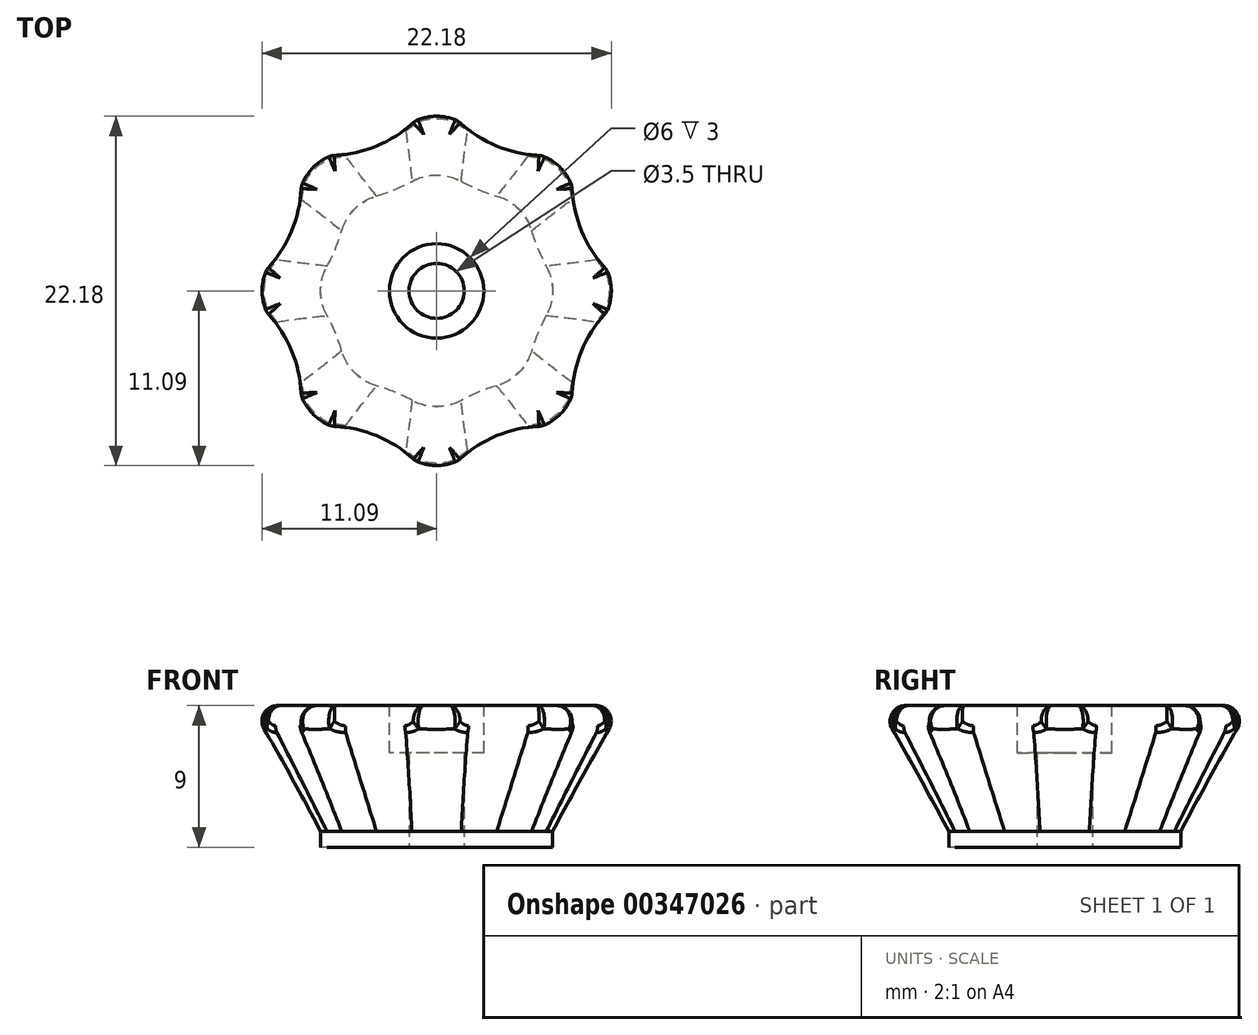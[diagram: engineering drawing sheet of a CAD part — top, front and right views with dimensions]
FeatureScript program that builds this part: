
annotation { "Feature Type Name" : "Feature", "Feature Type Description" : "" }
export const myFeature = defineFeature(function(context is Context, id is Id, definition is map)
    precondition{}
    {
        {
            var Q0;
            Q0=qCreatedBy(makeId("Top.planeOp"),FACE);
            var sketch = newSketch(context, id + "F0", { "sketchPlane" : qUnion([Q0])});
            skArc(sketch, "E0", {"start": v(0, 12.5) * mm, "mid": v(-8.84, 8.84) * mm, "end": v(-12.5, 0) * mm, "construction": true});
            skLineSegment(sketch, "E1", {"start": v(0, 0) * mm, "end": v(0, 89.09) * mm, "construction": true});
            skLineSegment(sketch, "E2", {"start": v(0, 0) * mm, "end": v(-93.87, 0) * mm, "construction": true});
            skArc(sketch, "E3", {"start": v(-8.84, 8.84) * mm, "mid": v(-3.81, 9.2) * mm, "end": v(0, 12.5) * mm});
            skArc(sketch, "E4", {"start": v(-12.5, 0) * mm, "mid": v(-9.2, 3.81) * mm, "end": v(-8.84, 8.84) * mm});
            skArc(sketch, "E5.MirrorCS", {"start": v(12.5, 0) * mm, "mid": v(9.2, 3.81) * mm, "end": v(8.84, 8.84) * mm});
            skArc(sketch, "E6.MirrorCS", {"start": v(8.84, 8.84) * mm, "mid": v(3.81, 9.2) * mm, "end": v(0, 12.5) * mm});
            skArc(sketch, "E7.MirrorCS", {"start": v(-12.5, 0) * mm, "mid": v(-9.2, -3.81) * mm, "end": v(-8.84, -8.84) * mm});
            skArc(sketch, "E8.MirrorCS", {"start": v(-8.84, -8.84) * mm, "mid": v(-3.81, -9.2) * mm, "end": v(0, -12.5) * mm});
            skArc(sketch, "E9.MirrorCS", {"start": v(8.84, -8.84) * mm, "mid": v(3.81, -9.2) * mm, "end": v(0, -12.5) * mm});
            skArc(sketch, "E10.MirrorCS", {"start": v(12.5, 0) * mm, "mid": v(9.2, -3.81) * mm, "end": v(8.84, -8.84) * mm});
            skSolve(sketch);
        }
        {
            var Q0;
            Q0=makeQuery(id+"F0.imprint","IMPRINT",FACE,{"disambiguationData":[TD([[makeQuery(id+"F0.imprint","IMPRINT",EDGE,{"derivedFrom":sQuery(id+"F0.wireOp",EDGE,"E3")}),-1.0]])]});
            extrude(context, id + "F1", {"entities" : qUnion([Q0]), "oppositeDirection" : true, "depth" : 8 * mm});
        }
        {
            var Q0;
            Q0=makeQuery(id+"F1.opExtrude","CAP_FACE",FACE,{"disambiguationData":[OSD([sQuery(id+"F0.wireOp",EDGE,"E3"),sQuery(id+"F0.wireOp",EDGE,"E4"),sQuery(id+"F0.wireOp",EDGE,"E5.MirrorCS"),sQuery(id+"F0.wireOp",EDGE,"E6.MirrorCS"),sQuery(id+"F0.wireOp",EDGE,"E7.MirrorCS"),sQuery(id+"F0.wireOp",EDGE,"E8.MirrorCS"),sQuery(id+"F0.wireOp",EDGE,"E9.MirrorCS"),sQuery(id+"F0.wireOp",EDGE,"E10.MirrorCS")])],"isStart":true});
            var sketch = newSketch(context, id + "F2", { "sketchPlane" : qUnion([Q0])});
            skCircle(sketch, "E11", {"center": v(0, 0) * mm, "radius": 3 * mm});
            skSolve(sketch);
        }
        {
            var Q0;
            Q0=makeQuery(id+"F2.imprint","IMPRINT",FACE,{"disambiguationData":[TD([[makeQuery(id+"F2.imprint","IMPRINT",EDGE,{"derivedFrom":sQuery(id+"F2.wireOp",EDGE,"E11")}),1.0]])]});
            extrude(context, id + "F3", {"entities" : qUnion([Q0]), "operationType" : NewBodyOperationType.REMOVE, "oppositeDirection" : true, "depth" : 3 * mm});
        }
        {
            var Q0;
            Q0=makeQuery(id+"F1.opExtrude","CAP_EDGE",EDGE,{"disambiguationData":[OSD([sQuery(id+"F0.wireOp",EDGE,"E6.MirrorCS")])],"isStart":false});
            var Q1;
            Q1=makeQuery(id+"F1.opExtrude","CAP_EDGE",EDGE,{"disambiguationData":[OSD([sQuery(id+"F0.wireOp",EDGE,"E3")])],"isStart":false});
            var Q2;
            Q2=makeQuery(id+"F1.opExtrude","CAP_EDGE",EDGE,{"disambiguationData":[OSD([sQuery(id+"F0.wireOp",EDGE,"E4")])],"isStart":false});
            var Q3;
            Q3=makeQuery(id+"F1.opExtrude","CAP_EDGE",EDGE,{"disambiguationData":[OSD([sQuery(id+"F0.wireOp",EDGE,"E7.MirrorCS")])],"isStart":false});
            var Q4;
            Q4=makeQuery(id+"F1.opExtrude","CAP_EDGE",EDGE,{"disambiguationData":[OSD([sQuery(id+"F0.wireOp",EDGE,"E8.MirrorCS")])],"isStart":false});
            var Q5;
            Q5=makeQuery(id+"F1.opExtrude","CAP_EDGE",EDGE,{"disambiguationData":[OSD([sQuery(id+"F0.wireOp",EDGE,"E10.MirrorCS")])],"isStart":false});
            var Q6;
            Q6=makeQuery(id+"F1.opExtrude","CAP_EDGE",EDGE,{"disambiguationData":[OSD([sQuery(id+"F0.wireOp",EDGE,"E9.MirrorCS")])],"isStart":false});
            var Q7;
            Q7=makeQuery(id+"F1.opExtrude","CAP_EDGE",EDGE,{"disambiguationData":[OSD([sQuery(id+"F0.wireOp",EDGE,"E5.MirrorCS")])],"isStart":false});
            chamfer(context, id + "F4", {"entities" : qUnion([Q0, Q1, Q2, Q3, Q4, Q5, Q6, Q7]), "chamferType" : ChamferType.TWO_OFFSETS, "width1" : 3 * mm, "oppositeDirection" : false, "width2" : 6.5 * mm, "tangentPropagation" : true});
        }
        {
            var Q0;
            Q0=makeQuery(id+"F1.opExtrude","SWEPT_EDGE",EDGE,{"disambiguationData":[OSD([sQuery(id+"F0.wireOp",EDGE,"E4"),sQuery(id+"F0.wireOp",EDGE,"E7.MirrorCS")])]});
            var Q1;
            Q1=makeQuery(id+"F1.opExtrude","SWEPT_EDGE",EDGE,{"disambiguationData":[OSD([sQuery(id+"F0.wireOp",EDGE,"E7.MirrorCS"),sQuery(id+"F0.wireOp",EDGE,"E8.MirrorCS")])]});
            var Q2;
            Q2=makeQuery(id+"F1.opExtrude","SWEPT_EDGE",EDGE,{"disambiguationData":[OSD([sQuery(id+"F0.wireOp",EDGE,"E8.MirrorCS"),sQuery(id+"F0.wireOp",EDGE,"E9.MirrorCS")])]});
            var Q3;
            Q3=makeQuery(id+"F1.opExtrude","SWEPT_EDGE",EDGE,{"disambiguationData":[OSD([sQuery(id+"F0.wireOp",EDGE,"E9.MirrorCS"),sQuery(id+"F0.wireOp",EDGE,"E10.MirrorCS")])]});
            var Q4;
            Q4=makeQuery(id+"F1.opExtrude","SWEPT_EDGE",EDGE,{"disambiguationData":[OSD([sQuery(id+"F0.wireOp",EDGE,"E5.MirrorCS"),sQuery(id+"F0.wireOp",EDGE,"E10.MirrorCS")])]});
            var Q5;
            Q5=makeQuery(id+"F1.opExtrude","SWEPT_EDGE",EDGE,{"disambiguationData":[OSD([sQuery(id+"F0.wireOp",EDGE,"E5.MirrorCS"),sQuery(id+"F0.wireOp",EDGE,"E6.MirrorCS")])]});
            var Q6;
            Q6=makeQuery(id+"F1.opExtrude","SWEPT_EDGE",EDGE,{"disambiguationData":[OSD([sQuery(id+"F0.wireOp",EDGE,"E3"),sQuery(id+"F0.wireOp",EDGE,"E6.MirrorCS")])]});
            var Q7;
            Q7=makeQuery(id+"F1.opExtrude","SWEPT_EDGE",EDGE,{"disambiguationData":[OSD([sQuery(id+"F0.wireOp",EDGE,"E3"),sQuery(id+"F0.wireOp",EDGE,"E4")])]});
            fillet(context, id + "F5", {"entities" : qUnion([Q0, Q1, Q2, Q3, Q4, Q5, Q6, Q7]), "radius" : 1.5 * mm, "tangentPropagation" : true, "allowEdgeOverflow" : false});
        }
        {
            var Q0;
            Q0=makeQuery(id+"F4.opChamfer","BLEND_EDGE",EDGE,{"blendedFrom":[makeQuery(id+"F1.opExtrude","CAP_EDGE",EDGE,{"disambiguationData":[OSD([sQuery(id+"F0.wireOp",EDGE,"E5.MirrorCS")])],"isStart":false}),makeQuery(id+"F1.opExtrude","CAP_EDGE",EDGE,{"disambiguationData":[OSD([sQuery(id+"F0.wireOp",EDGE,"E10.MirrorCS")])],"isStart":false})],"blendedInto":[]});
            var Q1;
            Q1=makeQuery(id+"F4.opChamfer","BLEND_EDGE",EDGE,{"blendedFrom":[makeQuery(id+"F1.opExtrude","CAP_EDGE",EDGE,{"disambiguationData":[OSD([sQuery(id+"F0.wireOp",EDGE,"E5.MirrorCS")])],"isStart":false}),makeQuery(id+"F1.opExtrude","CAP_EDGE",EDGE,{"disambiguationData":[OSD([sQuery(id+"F0.wireOp",EDGE,"E6.MirrorCS")])],"isStart":false})],"blendedInto":[]});
            var Q2;
            Q2=makeQuery(id+"F4.opChamfer","BLEND_EDGE",EDGE,{"blendedFrom":[makeQuery(id+"F1.opExtrude","CAP_EDGE",EDGE,{"disambiguationData":[OSD([sQuery(id+"F0.wireOp",EDGE,"E3")])],"isStart":false}),makeQuery(id+"F1.opExtrude","CAP_EDGE",EDGE,{"disambiguationData":[OSD([sQuery(id+"F0.wireOp",EDGE,"E6.MirrorCS")])],"isStart":false})],"blendedInto":[]});
            var Q3;
            Q3=makeQuery(id+"F4.opChamfer","BLEND_EDGE",EDGE,{"blendedFrom":[makeQuery(id+"F1.opExtrude","CAP_EDGE",EDGE,{"disambiguationData":[OSD([sQuery(id+"F0.wireOp",EDGE,"E3")])],"isStart":false}),makeQuery(id+"F1.opExtrude","CAP_EDGE",EDGE,{"disambiguationData":[OSD([sQuery(id+"F0.wireOp",EDGE,"E4")])],"isStart":false})],"blendedInto":[]});
            var Q4;
            Q4=makeQuery(id+"F4.opChamfer","BLEND_EDGE",EDGE,{"blendedFrom":[makeQuery(id+"F1.opExtrude","CAP_EDGE",EDGE,{"disambiguationData":[OSD([sQuery(id+"F0.wireOp",EDGE,"E4")])],"isStart":false}),makeQuery(id+"F1.opExtrude","CAP_EDGE",EDGE,{"disambiguationData":[OSD([sQuery(id+"F0.wireOp",EDGE,"E7.MirrorCS")])],"isStart":false})],"blendedInto":[]});
            var Q5;
            Q5=makeQuery(id+"F4.opChamfer","BLEND_EDGE",EDGE,{"blendedFrom":[makeQuery(id+"F1.opExtrude","CAP_EDGE",EDGE,{"disambiguationData":[OSD([sQuery(id+"F0.wireOp",EDGE,"E7.MirrorCS")])],"isStart":false}),makeQuery(id+"F1.opExtrude","CAP_EDGE",EDGE,{"disambiguationData":[OSD([sQuery(id+"F0.wireOp",EDGE,"E8.MirrorCS")])],"isStart":false})],"blendedInto":[]});
            var Q6;
            Q6=makeQuery(id+"F4.opChamfer","BLEND_EDGE",EDGE,{"blendedFrom":[makeQuery(id+"F1.opExtrude","CAP_EDGE",EDGE,{"disambiguationData":[OSD([sQuery(id+"F0.wireOp",EDGE,"E8.MirrorCS")])],"isStart":false}),makeQuery(id+"F1.opExtrude","CAP_EDGE",EDGE,{"disambiguationData":[OSD([sQuery(id+"F0.wireOp",EDGE,"E9.MirrorCS")])],"isStart":false})],"blendedInto":[]});
            var Q7;
            Q7=makeQuery(id+"F4.opChamfer","BLEND_EDGE",EDGE,{"blendedFrom":[makeQuery(id+"F1.opExtrude","CAP_EDGE",EDGE,{"disambiguationData":[OSD([sQuery(id+"F0.wireOp",EDGE,"E9.MirrorCS")])],"isStart":false}),makeQuery(id+"F1.opExtrude","CAP_EDGE",EDGE,{"disambiguationData":[OSD([sQuery(id+"F0.wireOp",EDGE,"E10.MirrorCS")])],"isStart":false})],"blendedInto":[]});
            fillet(context, id + "F6", {"entities" : qUnion([Q0, Q1, Q2, Q3, Q4, Q5, Q6, Q7]), "radius" : 3.58 * mm, "tangentPropagation" : true, "allowEdgeOverflow" : false});
        }
        {
            var Q0;
            Q0=makeQuery(id+"F1.opExtrude","CAP_FACE",FACE,{"disambiguationData":[OSD([sQuery(id+"F0.wireOp",EDGE,"E3"),sQuery(id+"F0.wireOp",EDGE,"E4"),sQuery(id+"F0.wireOp",EDGE,"E5.MirrorCS"),sQuery(id+"F0.wireOp",EDGE,"E6.MirrorCS"),sQuery(id+"F0.wireOp",EDGE,"E7.MirrorCS"),sQuery(id+"F0.wireOp",EDGE,"E8.MirrorCS"),sQuery(id+"F0.wireOp",EDGE,"E9.MirrorCS"),sQuery(id+"F0.wireOp",EDGE,"E10.MirrorCS")])],"isStart":false});
            extrude(context, id + "F7", {"entities" : qUnion([Q0]), "operationType" : NewBodyOperationType.ADD, "depth" : 1 * mm});
        }
        {
            var Q0;
            Q0=makeQuery(id+"F7.opExtrude","CAP_FACE",FACE,{"disambiguationData":[OSD([sQuery(id+"F0.wireOp",EDGE,"E3"),sQuery(id+"F0.wireOp",EDGE,"E4"),sQuery(id+"F0.wireOp",EDGE,"E5.MirrorCS"),sQuery(id+"F0.wireOp",EDGE,"E6.MirrorCS"),sQuery(id+"F0.wireOp",EDGE,"E7.MirrorCS"),sQuery(id+"F0.wireOp",EDGE,"E8.MirrorCS"),sQuery(id+"F0.wireOp",EDGE,"E9.MirrorCS"),sQuery(id+"F0.wireOp",EDGE,"E10.MirrorCS")])],"isStart":false});
            var sketch = newSketch(context, id + "F8", { "sketchPlane" : qUnion([Q0])});
            skPoint(sketch, "E12", {"position": v(0, 0) * mm});
            skSolve(sketch);
        }
        {
            var Q0;
            Q0=sQuery(id+"F8.wireOp",VERTEX,"E12");
            var Q1;
            Q1=makeQuery(id+"F1.opExtrude","SWEPT_BODY",BODY,{"disambiguationData":[OSD([sQuery(id+"F0.wireOp",EDGE,"E3"),sQuery(id+"F0.wireOp",EDGE,"E4"),sQuery(id+"F0.wireOp",EDGE,"E5.MirrorCS"),sQuery(id+"F0.wireOp",EDGE,"E6.MirrorCS"),sQuery(id+"F0.wireOp",EDGE,"E7.MirrorCS"),sQuery(id+"F0.wireOp",EDGE,"E8.MirrorCS"),sQuery(id+"F0.wireOp",EDGE,"E9.MirrorCS"),sQuery(id+"F0.wireOp",EDGE,"E10.MirrorCS")])]});
            hole(context, id + "F9", {"style" : HoleStyle.SIMPLE, "endStyle" : HoleEndStyle.THROUGH, "holeDiameter" : 3.5 * mm, "isTappedThrough" : true, "tappedDepth" : 12 * mm, "tapClearance" : 3, "locations" : qUnion([Q0]), "scope" : qUnion([Q1])});
        }
        {
            var Q0;
            Q0=makeQuery(id+"F1.opExtrude","CAP_EDGE",EDGE,{"disambiguationData":[OSD([sQuery(id+"F0.wireOp",EDGE,"E3")])],"isStart":true});
            var Q1;
            {var subQ0=sQuery(id+"F0.wireOp",EDGE,"E6.MirrorCS");var subQ1=sQuery(id+"F0.wireOp",EDGE,"E3");Q1=makeQuery(id+"F5.opFillet","BLEND_EDGE",EDGE,{"blendedFrom":[makeQuery(id+"F1.opExtrude","SWEPT_EDGE",EDGE,{"disambiguationData":[OSD([subQ1,subQ0])]}),makeQuery(id+"F1.opExtrude","CAP_FACE",FACE,{"disambiguationData":[OSD([subQ1,sQuery(id+"F0.wireOp",EDGE,"E4"),sQuery(id+"F0.wireOp",EDGE,"E5.MirrorCS"),subQ0,sQuery(id+"F0.wireOp",EDGE,"E7.MirrorCS"),sQuery(id+"F0.wireOp",EDGE,"E8.MirrorCS"),sQuery(id+"F0.wireOp",EDGE,"E9.MirrorCS"),sQuery(id+"F0.wireOp",EDGE,"E10.MirrorCS")])],"isStart":true})],"blendedInto":[makeQuery(id+"F1.opExtrude","CAP_FACE",FACE,{"disambiguationData":[OSD([subQ1,sQuery(id+"F0.wireOp",EDGE,"E4"),sQuery(id+"F0.wireOp",EDGE,"E5.MirrorCS"),subQ0,sQuery(id+"F0.wireOp",EDGE,"E7.MirrorCS"),sQuery(id+"F0.wireOp",EDGE,"E8.MirrorCS"),sQuery(id+"F0.wireOp",EDGE,"E9.MirrorCS"),sQuery(id+"F0.wireOp",EDGE,"E10.MirrorCS")])],"isStart":true})]});}
            var Q2;
            Q2=makeQuery(id+"F1.opExtrude","CAP_EDGE",EDGE,{"disambiguationData":[OSD([sQuery(id+"F0.wireOp",EDGE,"E6.MirrorCS")])],"isStart":true});
            var Q3;
            {var subQ0=sQuery(id+"F0.wireOp",EDGE,"E6.MirrorCS");var subQ1=sQuery(id+"F0.wireOp",EDGE,"E5.MirrorCS");Q3=makeQuery(id+"F5.opFillet","BLEND_EDGE",EDGE,{"blendedFrom":[makeQuery(id+"F1.opExtrude","SWEPT_EDGE",EDGE,{"disambiguationData":[OSD([subQ1,subQ0])]}),makeQuery(id+"F1.opExtrude","CAP_FACE",FACE,{"disambiguationData":[OSD([sQuery(id+"F0.wireOp",EDGE,"E3"),sQuery(id+"F0.wireOp",EDGE,"E4"),subQ1,subQ0,sQuery(id+"F0.wireOp",EDGE,"E7.MirrorCS"),sQuery(id+"F0.wireOp",EDGE,"E8.MirrorCS"),sQuery(id+"F0.wireOp",EDGE,"E9.MirrorCS"),sQuery(id+"F0.wireOp",EDGE,"E10.MirrorCS")])],"isStart":true})],"blendedInto":[makeQuery(id+"F1.opExtrude","CAP_FACE",FACE,{"disambiguationData":[OSD([sQuery(id+"F0.wireOp",EDGE,"E3"),sQuery(id+"F0.wireOp",EDGE,"E4"),subQ1,subQ0,sQuery(id+"F0.wireOp",EDGE,"E7.MirrorCS"),sQuery(id+"F0.wireOp",EDGE,"E8.MirrorCS"),sQuery(id+"F0.wireOp",EDGE,"E9.MirrorCS"),sQuery(id+"F0.wireOp",EDGE,"E10.MirrorCS")])],"isStart":true})]});}
            var Q4;
            Q4=makeQuery(id+"F1.opExtrude","CAP_EDGE",EDGE,{"disambiguationData":[OSD([sQuery(id+"F0.wireOp",EDGE,"E5.MirrorCS")])],"isStart":true});
            var Q5;
            {var subQ0=sQuery(id+"F0.wireOp",EDGE,"E10.MirrorCS");var subQ1=sQuery(id+"F0.wireOp",EDGE,"E5.MirrorCS");Q5=makeQuery(id+"F5.opFillet","BLEND_EDGE",EDGE,{"blendedFrom":[makeQuery(id+"F1.opExtrude","SWEPT_EDGE",EDGE,{"disambiguationData":[OSD([subQ1,subQ0])]}),makeQuery(id+"F1.opExtrude","CAP_FACE",FACE,{"disambiguationData":[OSD([sQuery(id+"F0.wireOp",EDGE,"E3"),sQuery(id+"F0.wireOp",EDGE,"E4"),subQ1,sQuery(id+"F0.wireOp",EDGE,"E6.MirrorCS"),sQuery(id+"F0.wireOp",EDGE,"E7.MirrorCS"),sQuery(id+"F0.wireOp",EDGE,"E8.MirrorCS"),sQuery(id+"F0.wireOp",EDGE,"E9.MirrorCS"),subQ0])],"isStart":true})],"blendedInto":[makeQuery(id+"F1.opExtrude","CAP_FACE",FACE,{"disambiguationData":[OSD([sQuery(id+"F0.wireOp",EDGE,"E3"),sQuery(id+"F0.wireOp",EDGE,"E4"),subQ1,sQuery(id+"F0.wireOp",EDGE,"E6.MirrorCS"),sQuery(id+"F0.wireOp",EDGE,"E7.MirrorCS"),sQuery(id+"F0.wireOp",EDGE,"E8.MirrorCS"),sQuery(id+"F0.wireOp",EDGE,"E9.MirrorCS"),subQ0])],"isStart":true})]});}
            var Q6;
            Q6=makeQuery(id+"F1.opExtrude","CAP_EDGE",EDGE,{"disambiguationData":[OSD([sQuery(id+"F0.wireOp",EDGE,"E10.MirrorCS")])],"isStart":true});
            var Q7;
            {var subQ0=sQuery(id+"F0.wireOp",EDGE,"E4");var subQ1=sQuery(id+"F0.wireOp",EDGE,"E3");Q7=makeQuery(id+"F5.opFillet","BLEND_EDGE",EDGE,{"blendedFrom":[makeQuery(id+"F1.opExtrude","SWEPT_EDGE",EDGE,{"disambiguationData":[OSD([subQ1,subQ0])]}),makeQuery(id+"F1.opExtrude","CAP_FACE",FACE,{"disambiguationData":[OSD([subQ1,subQ0,sQuery(id+"F0.wireOp",EDGE,"E5.MirrorCS"),sQuery(id+"F0.wireOp",EDGE,"E6.MirrorCS"),sQuery(id+"F0.wireOp",EDGE,"E7.MirrorCS"),sQuery(id+"F0.wireOp",EDGE,"E8.MirrorCS"),sQuery(id+"F0.wireOp",EDGE,"E9.MirrorCS"),sQuery(id+"F0.wireOp",EDGE,"E10.MirrorCS")])],"isStart":true})],"blendedInto":[makeQuery(id+"F1.opExtrude","CAP_FACE",FACE,{"disambiguationData":[OSD([subQ1,subQ0,sQuery(id+"F0.wireOp",EDGE,"E5.MirrorCS"),sQuery(id+"F0.wireOp",EDGE,"E6.MirrorCS"),sQuery(id+"F0.wireOp",EDGE,"E7.MirrorCS"),sQuery(id+"F0.wireOp",EDGE,"E8.MirrorCS"),sQuery(id+"F0.wireOp",EDGE,"E9.MirrorCS"),sQuery(id+"F0.wireOp",EDGE,"E10.MirrorCS")])],"isStart":true})]});}
            var Q8;
            Q8=makeQuery(id+"F1.opExtrude","CAP_EDGE",EDGE,{"disambiguationData":[OSD([sQuery(id+"F0.wireOp",EDGE,"E4")])],"isStart":true});
            var Q9;
            {var subQ0=sQuery(id+"F0.wireOp",EDGE,"E7.MirrorCS");var subQ1=sQuery(id+"F0.wireOp",EDGE,"E4");Q9=makeQuery(id+"F5.opFillet","BLEND_EDGE",EDGE,{"blendedFrom":[makeQuery(id+"F1.opExtrude","SWEPT_EDGE",EDGE,{"disambiguationData":[OSD([subQ1,subQ0])]}),makeQuery(id+"F1.opExtrude","CAP_FACE",FACE,{"disambiguationData":[OSD([sQuery(id+"F0.wireOp",EDGE,"E3"),subQ1,sQuery(id+"F0.wireOp",EDGE,"E5.MirrorCS"),sQuery(id+"F0.wireOp",EDGE,"E6.MirrorCS"),subQ0,sQuery(id+"F0.wireOp",EDGE,"E8.MirrorCS"),sQuery(id+"F0.wireOp",EDGE,"E9.MirrorCS"),sQuery(id+"F0.wireOp",EDGE,"E10.MirrorCS")])],"isStart":true})],"blendedInto":[makeQuery(id+"F1.opExtrude","CAP_FACE",FACE,{"disambiguationData":[OSD([sQuery(id+"F0.wireOp",EDGE,"E3"),subQ1,sQuery(id+"F0.wireOp",EDGE,"E5.MirrorCS"),sQuery(id+"F0.wireOp",EDGE,"E6.MirrorCS"),subQ0,sQuery(id+"F0.wireOp",EDGE,"E8.MirrorCS"),sQuery(id+"F0.wireOp",EDGE,"E9.MirrorCS"),sQuery(id+"F0.wireOp",EDGE,"E10.MirrorCS")])],"isStart":true})]});}
            var Q10;
            Q10=makeQuery(id+"F1.opExtrude","CAP_EDGE",EDGE,{"disambiguationData":[OSD([sQuery(id+"F0.wireOp",EDGE,"E7.MirrorCS")])],"isStart":true});
            var Q11;
            {var subQ0=sQuery(id+"F0.wireOp",EDGE,"E8.MirrorCS");var subQ1=sQuery(id+"F0.wireOp",EDGE,"E7.MirrorCS");Q11=makeQuery(id+"F5.opFillet","BLEND_EDGE",EDGE,{"blendedFrom":[makeQuery(id+"F1.opExtrude","SWEPT_EDGE",EDGE,{"disambiguationData":[OSD([subQ1,subQ0])]}),makeQuery(id+"F1.opExtrude","CAP_FACE",FACE,{"disambiguationData":[OSD([sQuery(id+"F0.wireOp",EDGE,"E3"),sQuery(id+"F0.wireOp",EDGE,"E4"),sQuery(id+"F0.wireOp",EDGE,"E5.MirrorCS"),sQuery(id+"F0.wireOp",EDGE,"E6.MirrorCS"),subQ1,subQ0,sQuery(id+"F0.wireOp",EDGE,"E9.MirrorCS"),sQuery(id+"F0.wireOp",EDGE,"E10.MirrorCS")])],"isStart":true})],"blendedInto":[makeQuery(id+"F1.opExtrude","CAP_FACE",FACE,{"disambiguationData":[OSD([sQuery(id+"F0.wireOp",EDGE,"E3"),sQuery(id+"F0.wireOp",EDGE,"E4"),sQuery(id+"F0.wireOp",EDGE,"E5.MirrorCS"),sQuery(id+"F0.wireOp",EDGE,"E6.MirrorCS"),subQ1,subQ0,sQuery(id+"F0.wireOp",EDGE,"E9.MirrorCS"),sQuery(id+"F0.wireOp",EDGE,"E10.MirrorCS")])],"isStart":true})]});}
            var Q12;
            Q12=makeQuery(id+"F1.opExtrude","CAP_EDGE",EDGE,{"disambiguationData":[OSD([sQuery(id+"F0.wireOp",EDGE,"E8.MirrorCS")])],"isStart":true});
            var Q13;
            {var subQ0=sQuery(id+"F0.wireOp",EDGE,"E9.MirrorCS");var subQ1=sQuery(id+"F0.wireOp",EDGE,"E8.MirrorCS");Q13=makeQuery(id+"F5.opFillet","BLEND_EDGE",EDGE,{"blendedFrom":[makeQuery(id+"F1.opExtrude","SWEPT_EDGE",EDGE,{"disambiguationData":[OSD([subQ1,subQ0])]}),makeQuery(id+"F1.opExtrude","CAP_FACE",FACE,{"disambiguationData":[OSD([sQuery(id+"F0.wireOp",EDGE,"E3"),sQuery(id+"F0.wireOp",EDGE,"E4"),sQuery(id+"F0.wireOp",EDGE,"E5.MirrorCS"),sQuery(id+"F0.wireOp",EDGE,"E6.MirrorCS"),sQuery(id+"F0.wireOp",EDGE,"E7.MirrorCS"),subQ1,subQ0,sQuery(id+"F0.wireOp",EDGE,"E10.MirrorCS")])],"isStart":true})],"blendedInto":[makeQuery(id+"F1.opExtrude","CAP_FACE",FACE,{"disambiguationData":[OSD([sQuery(id+"F0.wireOp",EDGE,"E3"),sQuery(id+"F0.wireOp",EDGE,"E4"),sQuery(id+"F0.wireOp",EDGE,"E5.MirrorCS"),sQuery(id+"F0.wireOp",EDGE,"E6.MirrorCS"),sQuery(id+"F0.wireOp",EDGE,"E7.MirrorCS"),subQ1,subQ0,sQuery(id+"F0.wireOp",EDGE,"E10.MirrorCS")])],"isStart":true})]});}
            var Q14;
            Q14=makeQuery(id+"F1.opExtrude","CAP_EDGE",EDGE,{"disambiguationData":[OSD([sQuery(id+"F0.wireOp",EDGE,"E9.MirrorCS")])],"isStart":true});
            var Q15;
            {var subQ0=sQuery(id+"F0.wireOp",EDGE,"E10.MirrorCS");var subQ1=sQuery(id+"F0.wireOp",EDGE,"E9.MirrorCS");Q15=makeQuery(id+"F5.opFillet","BLEND_EDGE",EDGE,{"blendedFrom":[makeQuery(id+"F1.opExtrude","SWEPT_EDGE",EDGE,{"disambiguationData":[OSD([subQ1,subQ0])]}),makeQuery(id+"F1.opExtrude","CAP_FACE",FACE,{"disambiguationData":[OSD([sQuery(id+"F0.wireOp",EDGE,"E3"),sQuery(id+"F0.wireOp",EDGE,"E4"),sQuery(id+"F0.wireOp",EDGE,"E5.MirrorCS"),sQuery(id+"F0.wireOp",EDGE,"E6.MirrorCS"),sQuery(id+"F0.wireOp",EDGE,"E7.MirrorCS"),sQuery(id+"F0.wireOp",EDGE,"E8.MirrorCS"),subQ1,subQ0])],"isStart":true})],"blendedInto":[makeQuery(id+"F1.opExtrude","CAP_FACE",FACE,{"disambiguationData":[OSD([sQuery(id+"F0.wireOp",EDGE,"E3"),sQuery(id+"F0.wireOp",EDGE,"E4"),sQuery(id+"F0.wireOp",EDGE,"E5.MirrorCS"),sQuery(id+"F0.wireOp",EDGE,"E6.MirrorCS"),sQuery(id+"F0.wireOp",EDGE,"E7.MirrorCS"),sQuery(id+"F0.wireOp",EDGE,"E8.MirrorCS"),subQ1,subQ0])],"isStart":true})]});}
            fillet(context, id + "F10", {"entities" : qUnion([Q0, Q1, Q2, Q3, Q4, Q5, Q6, Q7, Q8, Q9, Q10, Q11, Q12, Q13, Q14, Q15]), "radius" : 1 * mm, "tangentPropagation" : true, "allowEdgeOverflow" : false});
        }
        {
            var Q0;
            {var subQ0=sQuery(id+"F0.wireOp",EDGE,"E10.MirrorCS");var subQ1=sQuery(id+"F0.wireOp",EDGE,"E9.MirrorCS");Q0=makeQuery(id+"F6.opFillet","BLEND_EDGE",EDGE,{"blendedFrom":[makeQuery(id+"F4.opChamfer","BLEND_EDGE",EDGE,{"blendedFrom":[makeQuery(id+"F1.opExtrude","CAP_EDGE",EDGE,{"disambiguationData":[OSD([subQ1])],"isStart":false}),makeQuery(id+"F1.opExtrude","CAP_EDGE",EDGE,{"disambiguationData":[OSD([subQ0])],"isStart":false})],"blendedInto":[]}),makeQuery(id+"F5.opFillet","BLEND_FACE",FACE,{"disambiguationData":[OSD([subQ1,subQ0])]})],"blendedInto":[makeQuery(id+"F5.opFillet","BLEND_FACE",FACE,{"disambiguationData":[OSD([subQ1,subQ0])]})]});}
            var Q1;
            {var subQ0=sQuery(id+"F0.wireOp",EDGE,"E9.MirrorCS");Q1=makeQuery(id+"F4.opChamfer","BLEND_EDGE",EDGE,{"blendedFrom":[makeQuery(id+"F1.opExtrude","CAP_EDGE",EDGE,{"disambiguationData":[OSD([subQ0])],"isStart":false}),makeQuery(id+"F1.opExtrude","SWEPT_FACE",FACE,{"disambiguationData":[OSD([subQ0])]})],"blendedInto":[makeQuery(id+"F1.opExtrude","SWEPT_FACE",FACE,{"disambiguationData":[OSD([subQ0])]})]});}
            var Q2;
            {var subQ0=sQuery(id+"F0.wireOp",EDGE,"E9.MirrorCS");var subQ1=sQuery(id+"F0.wireOp",EDGE,"E8.MirrorCS");Q2=makeQuery(id+"F6.opFillet","BLEND_EDGE",EDGE,{"blendedFrom":[makeQuery(id+"F4.opChamfer","BLEND_EDGE",EDGE,{"blendedFrom":[makeQuery(id+"F1.opExtrude","CAP_EDGE",EDGE,{"disambiguationData":[OSD([subQ1])],"isStart":false}),makeQuery(id+"F1.opExtrude","CAP_EDGE",EDGE,{"disambiguationData":[OSD([subQ0])],"isStart":false})],"blendedInto":[]}),makeQuery(id+"F5.opFillet","BLEND_FACE",FACE,{"disambiguationData":[OSD([subQ1,subQ0])]})],"blendedInto":[makeQuery(id+"F5.opFillet","BLEND_FACE",FACE,{"disambiguationData":[OSD([subQ1,subQ0])]})]});}
            var Q3;
            {var subQ0=sQuery(id+"F0.wireOp",EDGE,"E8.MirrorCS");Q3=makeQuery(id+"F4.opChamfer","BLEND_EDGE",EDGE,{"blendedFrom":[makeQuery(id+"F1.opExtrude","CAP_EDGE",EDGE,{"disambiguationData":[OSD([subQ0])],"isStart":false}),makeQuery(id+"F1.opExtrude","SWEPT_FACE",FACE,{"disambiguationData":[OSD([subQ0])]})],"blendedInto":[makeQuery(id+"F1.opExtrude","SWEPT_FACE",FACE,{"disambiguationData":[OSD([subQ0])]})]});}
            var Q4;
            {var subQ0=sQuery(id+"F0.wireOp",EDGE,"E8.MirrorCS");var subQ1=sQuery(id+"F0.wireOp",EDGE,"E7.MirrorCS");Q4=makeQuery(id+"F6.opFillet","BLEND_EDGE",EDGE,{"blendedFrom":[makeQuery(id+"F4.opChamfer","BLEND_EDGE",EDGE,{"blendedFrom":[makeQuery(id+"F1.opExtrude","CAP_EDGE",EDGE,{"disambiguationData":[OSD([subQ1])],"isStart":false}),makeQuery(id+"F1.opExtrude","CAP_EDGE",EDGE,{"disambiguationData":[OSD([subQ0])],"isStart":false})],"blendedInto":[]}),makeQuery(id+"F5.opFillet","BLEND_FACE",FACE,{"disambiguationData":[OSD([subQ1,subQ0])]})],"blendedInto":[makeQuery(id+"F5.opFillet","BLEND_FACE",FACE,{"disambiguationData":[OSD([subQ1,subQ0])]})]});}
            var Q5;
            {var subQ0=sQuery(id+"F0.wireOp",EDGE,"E7.MirrorCS");Q5=makeQuery(id+"F4.opChamfer","BLEND_EDGE",EDGE,{"blendedFrom":[makeQuery(id+"F1.opExtrude","CAP_EDGE",EDGE,{"disambiguationData":[OSD([subQ0])],"isStart":false}),makeQuery(id+"F1.opExtrude","SWEPT_FACE",FACE,{"disambiguationData":[OSD([subQ0])]})],"blendedInto":[makeQuery(id+"F1.opExtrude","SWEPT_FACE",FACE,{"disambiguationData":[OSD([subQ0])]})]});}
            var Q6;
            {var subQ0=sQuery(id+"F0.wireOp",EDGE,"E7.MirrorCS");var subQ1=sQuery(id+"F0.wireOp",EDGE,"E4");Q6=makeQuery(id+"F6.opFillet","BLEND_EDGE",EDGE,{"blendedFrom":[makeQuery(id+"F4.opChamfer","BLEND_EDGE",EDGE,{"blendedFrom":[makeQuery(id+"F1.opExtrude","CAP_EDGE",EDGE,{"disambiguationData":[OSD([subQ1])],"isStart":false}),makeQuery(id+"F1.opExtrude","CAP_EDGE",EDGE,{"disambiguationData":[OSD([subQ0])],"isStart":false})],"blendedInto":[]}),makeQuery(id+"F5.opFillet","BLEND_FACE",FACE,{"disambiguationData":[OSD([subQ1,subQ0])]})],"blendedInto":[makeQuery(id+"F5.opFillet","BLEND_FACE",FACE,{"disambiguationData":[OSD([subQ1,subQ0])]})]});}
            var Q7;
            {var subQ0=sQuery(id+"F0.wireOp",EDGE,"E4");Q7=makeQuery(id+"F4.opChamfer","BLEND_EDGE",EDGE,{"blendedFrom":[makeQuery(id+"F1.opExtrude","CAP_EDGE",EDGE,{"disambiguationData":[OSD([subQ0])],"isStart":false}),makeQuery(id+"F1.opExtrude","SWEPT_FACE",FACE,{"disambiguationData":[OSD([subQ0])]})],"blendedInto":[makeQuery(id+"F1.opExtrude","SWEPT_FACE",FACE,{"disambiguationData":[OSD([subQ0])]})]});}
            var Q8;
            {var subQ0=sQuery(id+"F0.wireOp",EDGE,"E4");var subQ1=sQuery(id+"F0.wireOp",EDGE,"E3");Q8=makeQuery(id+"F6.opFillet","BLEND_EDGE",EDGE,{"blendedFrom":[makeQuery(id+"F4.opChamfer","BLEND_EDGE",EDGE,{"blendedFrom":[makeQuery(id+"F1.opExtrude","CAP_EDGE",EDGE,{"disambiguationData":[OSD([subQ1])],"isStart":false}),makeQuery(id+"F1.opExtrude","CAP_EDGE",EDGE,{"disambiguationData":[OSD([subQ0])],"isStart":false})],"blendedInto":[]}),makeQuery(id+"F5.opFillet","BLEND_FACE",FACE,{"disambiguationData":[OSD([subQ1,subQ0])]})],"blendedInto":[makeQuery(id+"F5.opFillet","BLEND_FACE",FACE,{"disambiguationData":[OSD([subQ1,subQ0])]})]});}
            var Q9;
            {var subQ0=sQuery(id+"F0.wireOp",EDGE,"E3");Q9=makeQuery(id+"F4.opChamfer","BLEND_EDGE",EDGE,{"blendedFrom":[makeQuery(id+"F1.opExtrude","CAP_EDGE",EDGE,{"disambiguationData":[OSD([subQ0])],"isStart":false}),makeQuery(id+"F1.opExtrude","SWEPT_FACE",FACE,{"disambiguationData":[OSD([subQ0])]})],"blendedInto":[makeQuery(id+"F1.opExtrude","SWEPT_FACE",FACE,{"disambiguationData":[OSD([subQ0])]})]});}
            var Q10;
            {var subQ0=sQuery(id+"F0.wireOp",EDGE,"E10.MirrorCS");Q10=makeQuery(id+"F4.opChamfer","BLEND_EDGE",EDGE,{"blendedFrom":[makeQuery(id+"F1.opExtrude","CAP_EDGE",EDGE,{"disambiguationData":[OSD([subQ0])],"isStart":false}),makeQuery(id+"F1.opExtrude","SWEPT_FACE",FACE,{"disambiguationData":[OSD([subQ0])]})],"blendedInto":[makeQuery(id+"F1.opExtrude","SWEPT_FACE",FACE,{"disambiguationData":[OSD([subQ0])]})]});}
            var Q11;
            {var subQ0=sQuery(id+"F0.wireOp",EDGE,"E5.MirrorCS");Q11=makeQuery(id+"F4.opChamfer","BLEND_EDGE",EDGE,{"blendedFrom":[makeQuery(id+"F1.opExtrude","CAP_EDGE",EDGE,{"disambiguationData":[OSD([subQ0])],"isStart":false}),makeQuery(id+"F1.opExtrude","SWEPT_FACE",FACE,{"disambiguationData":[OSD([subQ0])]})],"blendedInto":[makeQuery(id+"F1.opExtrude","SWEPT_FACE",FACE,{"disambiguationData":[OSD([subQ0])]})]});}
            var Q12;
            {var subQ0=sQuery(id+"F0.wireOp",EDGE,"E6.MirrorCS");Q12=makeQuery(id+"F4.opChamfer","BLEND_EDGE",EDGE,{"blendedFrom":[makeQuery(id+"F1.opExtrude","CAP_EDGE",EDGE,{"disambiguationData":[OSD([subQ0])],"isStart":false}),makeQuery(id+"F1.opExtrude","SWEPT_FACE",FACE,{"disambiguationData":[OSD([subQ0])]})],"blendedInto":[makeQuery(id+"F1.opExtrude","SWEPT_FACE",FACE,{"disambiguationData":[OSD([subQ0])]})]});}
            var Q13;
            {var subQ0=sQuery(id+"F0.wireOp",EDGE,"E6.MirrorCS");var subQ1=sQuery(id+"F0.wireOp",EDGE,"E3");Q13=makeQuery(id+"F6.opFillet","BLEND_EDGE",EDGE,{"blendedFrom":[makeQuery(id+"F4.opChamfer","BLEND_EDGE",EDGE,{"blendedFrom":[makeQuery(id+"F1.opExtrude","CAP_EDGE",EDGE,{"disambiguationData":[OSD([subQ1])],"isStart":false}),makeQuery(id+"F1.opExtrude","CAP_EDGE",EDGE,{"disambiguationData":[OSD([subQ0])],"isStart":false})],"blendedInto":[]}),makeQuery(id+"F5.opFillet","BLEND_FACE",FACE,{"disambiguationData":[OSD([subQ1,subQ0])]})],"blendedInto":[makeQuery(id+"F5.opFillet","BLEND_FACE",FACE,{"disambiguationData":[OSD([subQ1,subQ0])]})]});}
            var Q14;
            {var subQ0=sQuery(id+"F0.wireOp",EDGE,"E6.MirrorCS");var subQ1=sQuery(id+"F0.wireOp",EDGE,"E5.MirrorCS");Q14=makeQuery(id+"F6.opFillet","BLEND_EDGE",EDGE,{"blendedFrom":[makeQuery(id+"F4.opChamfer","BLEND_EDGE",EDGE,{"blendedFrom":[makeQuery(id+"F1.opExtrude","CAP_EDGE",EDGE,{"disambiguationData":[OSD([subQ1])],"isStart":false}),makeQuery(id+"F1.opExtrude","CAP_EDGE",EDGE,{"disambiguationData":[OSD([subQ0])],"isStart":false})],"blendedInto":[]}),makeQuery(id+"F5.opFillet","BLEND_FACE",FACE,{"disambiguationData":[OSD([subQ1,subQ0])]})],"blendedInto":[makeQuery(id+"F5.opFillet","BLEND_FACE",FACE,{"disambiguationData":[OSD([subQ1,subQ0])]})]});}
            var Q15;
            {var subQ0=sQuery(id+"F0.wireOp",EDGE,"E10.MirrorCS");var subQ1=sQuery(id+"F0.wireOp",EDGE,"E5.MirrorCS");Q15=makeQuery(id+"F6.opFillet","BLEND_EDGE",EDGE,{"blendedFrom":[makeQuery(id+"F4.opChamfer","BLEND_EDGE",EDGE,{"blendedFrom":[makeQuery(id+"F1.opExtrude","CAP_EDGE",EDGE,{"disambiguationData":[OSD([subQ1])],"isStart":false}),makeQuery(id+"F1.opExtrude","CAP_EDGE",EDGE,{"disambiguationData":[OSD([subQ0])],"isStart":false})],"blendedInto":[]}),makeQuery(id+"F5.opFillet","BLEND_FACE",FACE,{"disambiguationData":[OSD([subQ1,subQ0])]})],"blendedInto":[makeQuery(id+"F5.opFillet","BLEND_FACE",FACE,{"disambiguationData":[OSD([subQ1,subQ0])]})]});}
            fillet(context, id + "F11", {"entities" : qUnion([Q0, Q1, Q2, Q3, Q4, Q5, Q6, Q7, Q8, Q9, Q10, Q11, Q12, Q13, Q14, Q15]), "radius" : 1 * mm, "tangentPropagation" : true, "allowEdgeOverflow" : false});
        }
    });
